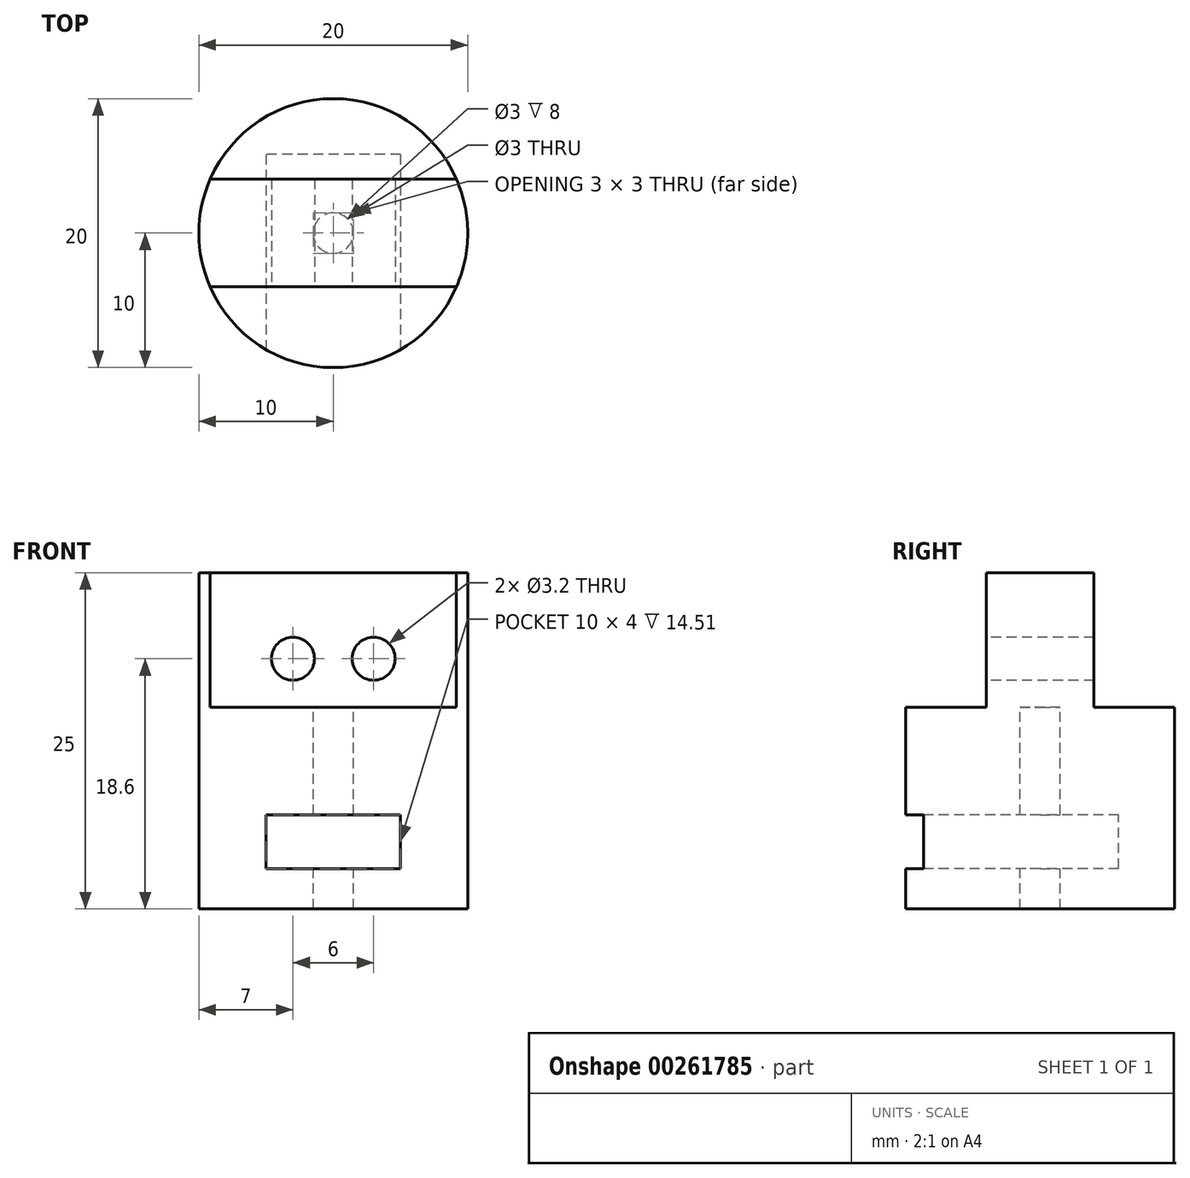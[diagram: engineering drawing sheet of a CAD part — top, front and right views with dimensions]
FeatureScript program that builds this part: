
annotation { "Feature Type Name" : "Feature", "Feature Type Description" : "" }
export const myFeature = defineFeature(function(context is Context, id is Id, definition is map)
    precondition{}
    {
        {
            var Q0;
            Q0=qCreatedBy(makeId("Top.planeOp"),FACE);
            var sketch = newSketch(context, id + "F0", { "sketchPlane" : qUnion([Q0])});
            skCircle(sketch, "E0", {"center": v(0, 0) * mm, "radius": 10 * mm});
            skCircle(sketch, "E1", {"center": v(0, 0) * mm, "radius": 1.5 * mm});
            skLineSegment(sketch, "E2", {"start": v(-14.48, 0) * mm, "end": v(16.3, 0) * mm, "construction": true});
            skLineSegment(sketch, "E3", {"start": v(-9.17, 4) * mm, "end": v(9.17, 4) * mm});
            skLineSegment(sketch, "E4", {"start": v(-9.17, -4) * mm, "end": v(9.17, -4) * mm});
            skSolve(sketch);
        }
        {
            var Q0;
            Q0=makeQuery(id+"F0.imprint","IMPRINT",FACE,{"disambiguationData":[TD([[makeQuery(id+"F0.imprint","IMPRINT",EDGE,{"derivedFrom":sQuery(id+"F0.wireOp",EDGE,"E1")}),-1.0]])]});
            var Q1;
            {var subQ0=sQuery(id+"F0.wireOp",EDGE,"E4");Q1=makeQuery(id+"F0.imprint","IMPRINT",FACE,{"disambiguationData":[TD([[makeQuery(id+"F0.imprint","IMPRINT",EDGE,{"derivedFrom":subQ0}),-1.0]])]});}
            var Q2;
            {var subQ0=sQuery(id+"F0.wireOp",EDGE,"E3");Q2=makeQuery(id+"F0.imprint","IMPRINT",FACE,{"disambiguationData":[TD([[makeQuery(id+"F0.imprint","IMPRINT",EDGE,{"derivedFrom":subQ0}),1.0]])]});}
            extrude(context, id + "F1", {"entities" : qUnion([Q0, Q1, Q2]), "oppositeDirection" : true, "depth" : 15 * mm});
        }
        {
            var Q0;
            Q0=qCreatedBy(makeId("Front.planeOp"),FACE);
            cPlane(context, id + "F2", {"entities" : qUnion([Q0]), "cplaneType" : CPlaneType.OFFSET, "offset" : 40 * mm, "width" : 150 * mm, "height" : 150 * mm});
        }
        {
            var Q0;
            Q0=qCreatedBy(id+"F2.planeOp",FACE);
            var sketch = newSketch(context, id + "F3", { "sketchPlane" : qUnion([Q0])});
            skLineSegment(sketch, "E5", {"start": v(0, -17.24) * mm, "end": v(0, -6.84) * mm, "construction": true});
            skLineSegment(sketch, "E6.bottom", {"start": v(-5, -8) * mm, "end": v(5, -8) * mm});
            skLineSegment(sketch, "E6.top", {"start": v(-5, -12) * mm, "end": v(5, -12) * mm});
            skLineSegment(sketch, "E6.left", {"start": v(-5, -8) * mm, "end": v(-5, -12) * mm});
            skLineSegment(sketch, "E6.right", {"start": v(5, -8) * mm, "end": v(5, -12) * mm});
            skSolve(sketch);
        }
        {
            var Q0;
            Q0=qCreatedBy(makeId("Front.planeOp"),FACE);
            cPlane(context, id + "F4", {"entities" : qUnion([Q0]), "cplaneType" : CPlaneType.OFFSET, "offset" : (11.7 / 2) * mm, "oppositeDirection" : true, "width" : 150 * mm, "height" : 150 * mm});
        }
        {
            var Q0;
            Q0 = qSketchRegion(id + "F3", true);
            var Q1;
            Q1=qCreatedBy(id+"F4.planeOp",FACE);
            extrude(context, id + "F5", {"entities" : qUnion([Q0]), "operationType" : NewBodyOperationType.REMOVE, "endBound" : BoundingType.UP_TO_SURFACE, "oppositeDirection" : true, "endBoundEntityFace" : qUnion([Q1]), "depth" : 25 * mm});
        }
        {
            var Q0;
            Q0=makeQuery(id+"F0.imprint","IMPRINT",FACE,{"disambiguationData":[TD([[makeQuery(id+"F0.imprint","IMPRINT",EDGE,{"derivedFrom":sQuery(id+"F0.wireOp",EDGE,"E1")}),1.0]])]});
            var Q1;
            Q1=makeQuery(id+"F0.imprint","IMPRINT",FACE,{"disambiguationData":[TD([[makeQuery(id+"F0.imprint","IMPRINT",EDGE,{"derivedFrom":sQuery(id+"F0.wireOp",EDGE,"E1")}),-1.0]])]});
            extrude(context, id + "F6", {"entities" : qUnion([Q0, Q1]), "operationType" : NewBodyOperationType.ADD, "depth" : 10 * mm});
        }
        {
            var Q0;
            Q0=makeQuery(id+"F6.opExtrude","SWEPT_FACE",FACE,{"disambiguationData":[OSD([sQuery(id+"F0.wireOp",EDGE,"E4")])]});
            var sketch = newSketch(context, id + "F7", { "sketchPlane" : qUnion([Q0])});
            skCircle(sketch, "E7", {"center": v(-3, 3.6) * mm, "radius": 1.6 * mm});
            skCircle(sketch, "E8", {"center": v(3, 3.6) * mm, "radius": 1.6 * mm});
            skLineSegment(sketch, "E9", {"start": v(-5.48, 3.6) * mm, "end": v(9.36, 3.6) * mm, "construction": true});
            skLineSegment(sketch, "E10", {"start": v(0, 1.14) * mm, "end": v(0, 10.6) * mm, "construction": true});
            skSolve(sketch);
        }
        {
            var Q0;
            Q0 = qSketchRegion(id + "F7", true);
            extrude(context, id + "F8", {"entities" : qUnion([Q0]), "operationType" : NewBodyOperationType.REMOVE, "endBound" : BoundingType.THROUGH_ALL, "oppositeDirection" : true, "depth" : 25 * mm});
        }
    });
